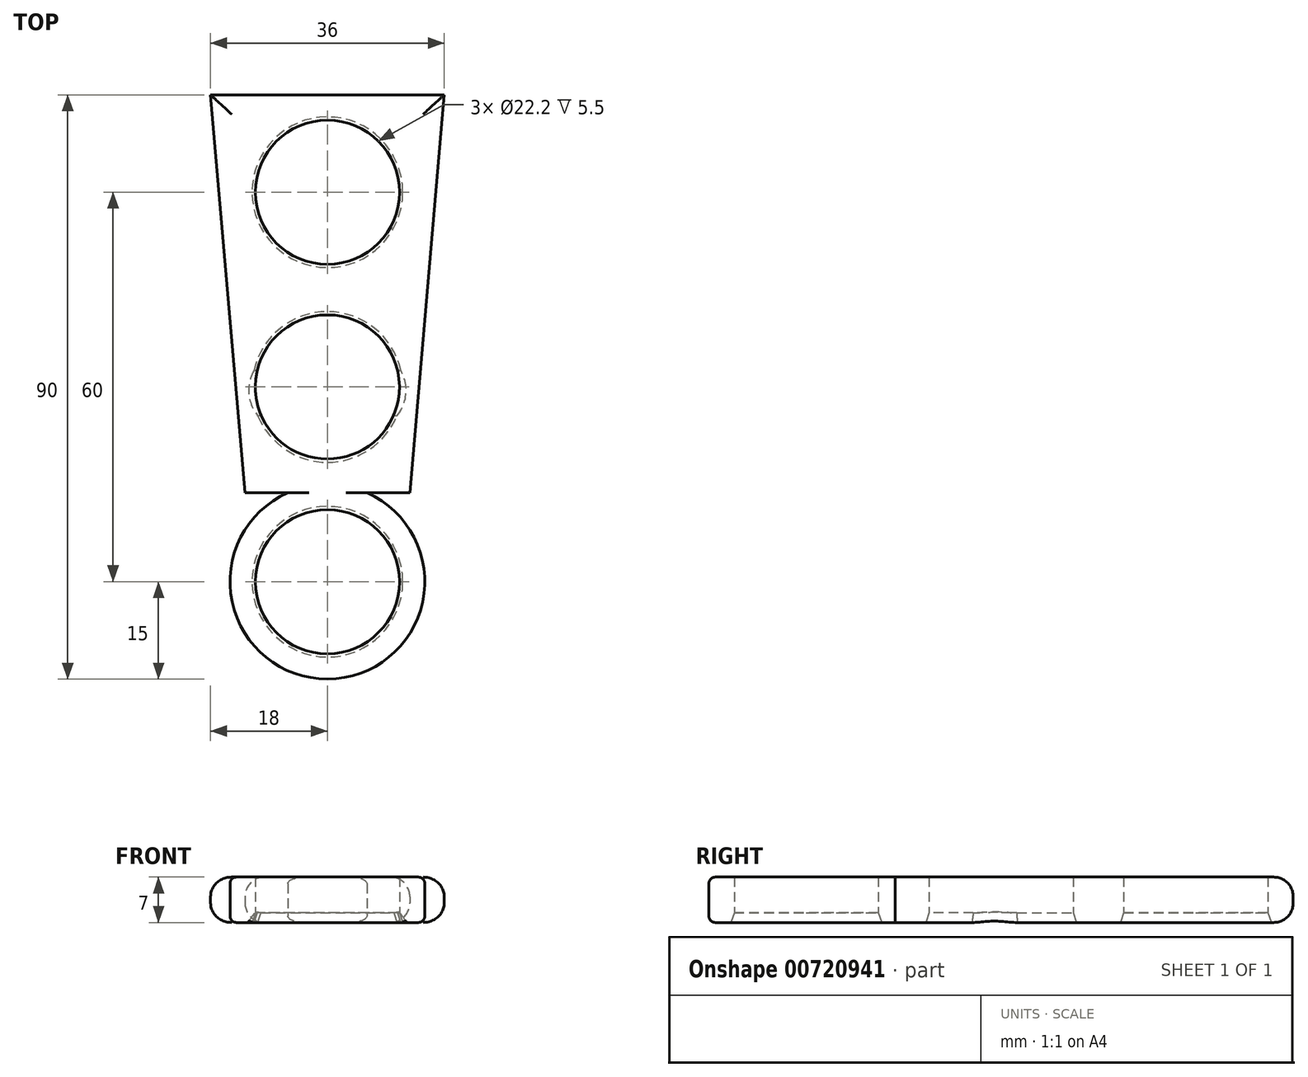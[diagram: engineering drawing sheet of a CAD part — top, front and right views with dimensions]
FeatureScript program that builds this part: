
annotation { "Feature Type Name" : "Feature", "Feature Type Description" : "" }
export const myFeature = defineFeature(function(context is Context, id is Id, definition is map)
    precondition{}
    {
        {
            var Q0;
            Q0=qCreatedBy(makeId("Top.planeOp"),FACE);
            var sketch = newSketch(context, id + "F0", { "sketchPlane" : qUnion([Q0])});
            skLineSegment(sketch, "E0", {"start": v(-18, 45) * mm, "end": v(18, 45) * mm});
            skLineSegment(sketch, "E1", {"start": v(18, 45) * mm, "end": v(12.7, -16.3) * mm});
            skLineSegment(sketch, "E2", {"start": v(12.7, -16.3) * mm, "end": v(-12.7, -16.3) * mm});
            skLineSegment(sketch, "E3", {"start": v(-12.7, -16.3) * mm, "end": v(-18, 45) * mm});
            skLineSegment(sketch, "E4", {"start": v(0, 45) * mm, "end": v(0, -16.3) * mm, "construction": true});
            skCircle(sketch, "E5", {"center": v(0, 0) * mm, "radius": 11.1 * mm});
            skArc(sketch, "E6", {"start": v(-6.1, -16.3) * mm, "mid": v(0, -45) * mm, "end": v(6.1, -16.3) * mm});
            skCircle(sketch, "E7", {"center": v(0, -30) * mm, "radius": 11.1 * mm});
            skCircle(sketch, "E8", {"center": v(0, 30) * mm, "radius": 11.1 * mm});
            skSolve(sketch);
        }
        {
            var Q0;
            Q0=makeQuery(id+"F0.imprint","IMPRINT",FACE,{"disambiguationData":[TD([[makeQuery(id+"F0.imprint","IMPRINT",EDGE,{"derivedFrom":sQuery(id+"F0.wireOp",EDGE,"E0")}),-1.0]])]});
            var Q1;
            {var subQ0=sQuery(id+"F0.wireOp",EDGE,"E6");Q1=makeQuery(id+"F0.imprint","IMPRINT",FACE,{"disambiguationData":[TD([[makeQuery(id+"F0.imprint","IMPRINT",EDGE,{"derivedFrom":subQ0}),1.0]])]});}
            extrude(context, id + "F1", {"entities" : qUnion([Q0, Q1]), "depth" : 7 * mm});
        }
        {
            var Q0;
            Q0=makeQuery(id+"F1.opExtrude","CAP_EDGE",EDGE,{"disambiguationData":[OSD([sQuery(id+"F0.wireOp",EDGE,"E0")])],"isStart":false});
            var Q1;
            Q1=makeQuery(id+"F1.opExtrude","CAP_EDGE",EDGE,{"disambiguationData":[OSD([sQuery(id+"F0.wireOp",EDGE,"E3")])],"isStart":false});
            var Q2;
            Q2=makeQuery(id+"F1.opExtrude","CAP_EDGE",EDGE,{"disambiguationData":[OSD([sQuery(id+"F0.wireOp",EDGE,"E1")])],"isStart":false});
            var Q3;
            Q3=makeQuery(id+"F1.opExtrude","CAP_EDGE",EDGE,{"disambiguationData":[OSD([sQuery(id+"F0.wireOp",EDGE,"E1")])],"isStart":true});
            var Q4;
            Q4=makeQuery(id+"F1.opExtrude","CAP_EDGE",EDGE,{"disambiguationData":[OSD([sQuery(id+"F0.wireOp",EDGE,"E0")])],"isStart":true});
            var Q5;
            Q5=makeQuery(id+"F1.opExtrude","CAP_EDGE",EDGE,{"disambiguationData":[OSD([sQuery(id+"F0.wireOp",EDGE,"E3")])],"isStart":true});
            fillet(context, id + "F2", {"entities" : qUnion([Q0, Q1, Q2, Q3, Q4, Q5]), "radius" : 3 * mm, "tangentPropagation" : true, "allowEdgeOverflow" : false});
        }
        {
            var Q0;
            Q0=makeQuery(id+"F1.opExtrude","CAP_EDGE",EDGE,{"disambiguationData":[OSD([sQuery(id+"F0.wireOp",EDGE,"E6")])],"isStart":false});
            var Q1;
            Q1=makeQuery(id+"F1.opExtrude","CAP_EDGE",EDGE,{"disambiguationData":[OSD([sQuery(id+"F0.wireOp",EDGE,"E6")])],"isStart":true});
            fillet(context, id + "F3", {"entities" : qUnion([Q0, Q1]), "radius" : 1 * mm, "tangentPropagation" : true, "allowEdgeOverflow" : false});
        }
        {
            var Q0;
            Q0=makeQuery(id+"F1.opExtrude","CAP_EDGE",EDGE,{"disambiguationData":[OSD([sQuery(id+"F0.wireOp",EDGE,"E5")])],"isStart":true});
            var Q1;
            Q1=makeQuery(id+"F1.opExtrude","CAP_EDGE",EDGE,{"disambiguationData":[OSD([sQuery(id+"F0.wireOp",EDGE,"E8")])],"isStart":true});
            var Q2;
            Q2=makeQuery(id+"F1.opExtrude","CAP_EDGE",EDGE,{"disambiguationData":[OSD([sQuery(id+"F0.wireOp",EDGE,"E7")])],"isStart":true});
            chamfer(context, id + "F4", {"entities" : qUnion([Q0, Q1, Q2]), "chamferType" : ChamferType.TWO_OFFSETS, "width1" : .5 * mm, "oppositeDirection" : false, "width2" : 1.5 * mm, "tangentPropagation" : true});
        }
    });
